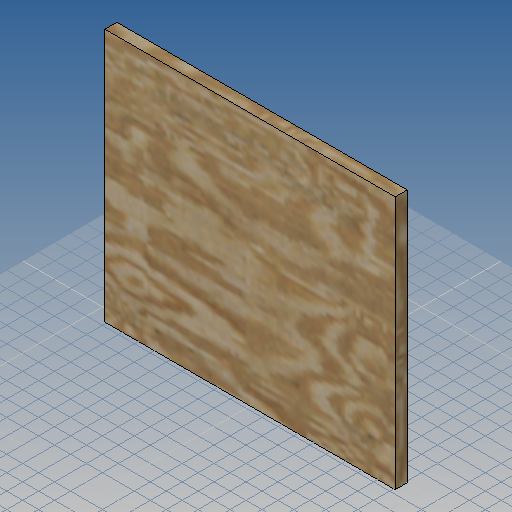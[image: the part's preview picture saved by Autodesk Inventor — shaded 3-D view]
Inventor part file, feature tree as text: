
AUTODESK INVENTOR PART (.ipt)
format: ipt  version: 2019 (Build 230136000, 136)  size: 295,936 bytes
history: native  units: mm
features: other x1, extrude x1, sketch x1
ambient origin geometry x8: Origin, YZ Plane, XZ Plane, XY Plane, X Axis, Y Axis, Z Axis, Center Point
bodies: Volumenkörper1 (feature_tree)
feature tree (3):
  other  "<userpath>\OneDrive\Dokumente\Inventor\Absauganlage\Absauganlage_Params.xlsx"
  extrude  "Extrusion1"  Depth=364.0mm
  sketch  "Skizze1"  dims[d0=318.0mm d1=364.0mm d2=15.0mm d3=0.0mm]
